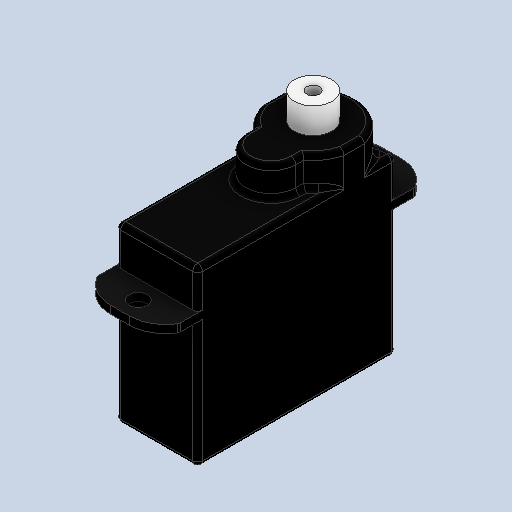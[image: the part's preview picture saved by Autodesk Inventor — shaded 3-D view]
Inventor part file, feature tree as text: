
AUTODESK INVENTOR PART (.ipt)
format: ipt  version: 2023 (Build 270158000, 158)  size: 908,800 bytes
history: native  units: in
note: dims shown in document units (in); Inventor stores cm internally (conversion verified against a paired STEP export)
features: extrude x7, projected_geometry x6, sketch x5, fillet x4
ambient origin geometry x8: Origin, YZ Plane, XZ Plane, XY Plane, X Axis, Y Axis, Z Axis, Center Point
bodies: Solid1 (feature_tree)
feature tree (22):
  extrude  "Extrusion1"  Depth=0.7874in
  extrude  "Extrusion2"  Depth=0.3346in
  extrude  "Extrusion3"  Depth=0.1181in TaperAngle=0.0deg
  sketch  "Sketch4"  dims[d9=0.1496in d10=0.0512in]
  extrude  "Extrusion4"  Depth=0.0512in
  extrude  "Extrusion5"  Depth=0.0197in TaperAngle=0.0deg
  fillet  "Fillet1"  Radius=0.1457in
  fillet  "Fillet2"  Radius=0.126in
  fillet  "Fillet3"  Radius=0.126in
  sketch  "Sketch5"  dims[d12=53.1496in d14=360.0deg d16=0.1024in d17=0.0in d18=0.1457in d19=0.126in d20=0.126in d21=0.1831in d22=0.0in d23=0.1516in d24=0.0in d25=0.0197in d26=0.0197in d27=0.0197in d28=0.1516in d29=0.0in d30=0.3937in d31=0.0in d32=0.0197in]
  extrude  "Extrusion6"  Depth=0.0197in TaperAngle=0.0deg
  extrude  "Extrusion7"  Depth=0.0197in TaperAngle=0.0deg
  fillet  "Fillet4"  Radius=0.0197in
  sketch  "Sketch1"  dims[d0=0.3248in d1=0.7874in]
  sketch  "Sketch2"  dims[d2=0.689in d3=0.0in d5=0.3346in]
  projected_geometry  "Projected Loop1"
  sketch  "Sketch3"  dims[d6=0.1969in d7=0.1181in d8=0.0in]
  projected_geometry  "Projected Loop2"
  projected_geometry  "Projected Loop3"
  projected_geometry  "Projected Loop4"
  projected_geometry  "Projected Loop5"
  projected_geometry  "Projected Loop6"
